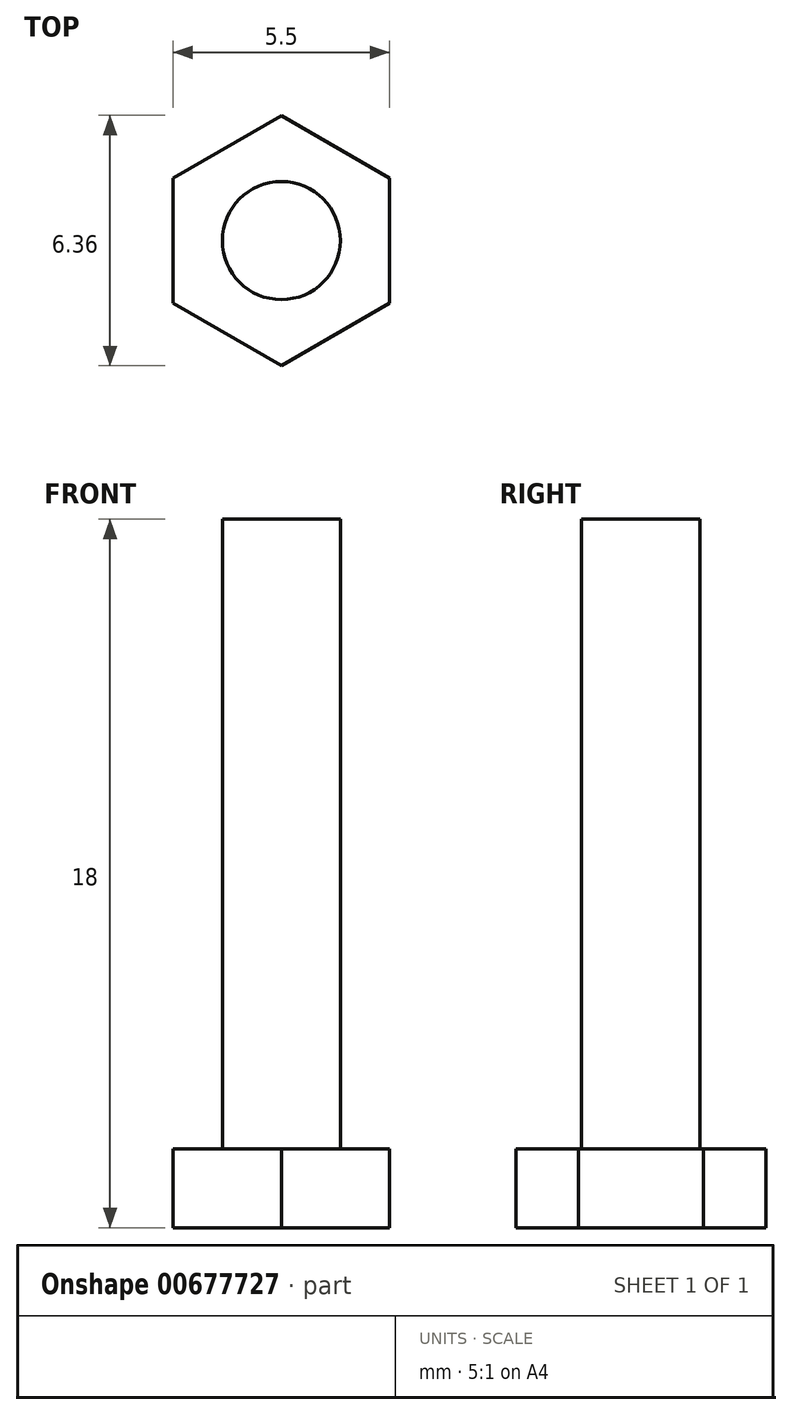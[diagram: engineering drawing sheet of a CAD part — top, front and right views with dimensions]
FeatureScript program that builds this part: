
annotation { "Feature Type Name" : "Feature", "Feature Type Description" : "" }
export const myFeature = defineFeature(function(context is Context, id is Id, definition is map)
    precondition{}
    {
        {
            var Q0;
            Q0=qCreatedBy(makeId("Top.planeOp"),FACE);
            var sketch = newSketch(context, id + "F0", { "sketchPlane" : qUnion([Q0])});
            skCircle(sketch, "E0.cCircle", {"center": v(0, 0) * mm, "radius": 2.75 * mm, "construction": true});
            skLineSegment(sketch, "E0.0", {"start": v(2.75, 1.59) * mm, "end": v(2.75, -1.59) * mm});
            skLineSegment(sketch, "E0.1", {"start": v(2.75, -1.59) * mm, "end": v(0, -3.18) * mm});
            skLineSegment(sketch, "E0.2", {"start": v(0, -3.18) * mm, "end": v(-2.75, -1.59) * mm});
            skLineSegment(sketch, "E0.3", {"start": v(-2.75, -1.59) * mm, "end": v(-2.75, 1.59) * mm});
            skLineSegment(sketch, "E0.4", {"start": v(-2.75, 1.59) * mm, "end": v(0, 3.18) * mm});
            skLineSegment(sketch, "E0.5", {"start": v(0, 3.18) * mm, "end": v(2.75, 1.59) * mm});
            skPoint(sketch, "E0.0.midPoint", {"position": v(2.75, 0) * mm});
            skSolve(sketch);
        }
        {
            var Q0;
            Q0=makeQuery(id+"F0.imprint","IMPRINT",FACE,{"disambiguationData":[TD([[makeQuery(id+"F0.imprint","IMPRINT",EDGE,{"derivedFrom":sQuery(id+"F0.wireOp",EDGE,"E0.0")}),-1.0]])]});
            extrude(context, id + "F1", {"entities" : qUnion([Q0]), "depth" : 2 * mm, "offsetDistance" : 25.4 * mm});
        }
        {
            var Q0;
            Q0=makeQuery(id+"F1.opExtrude","CAP_FACE",FACE,{"disambiguationData":[OSD([sQuery(id+"F0.wireOp",EDGE,"E0.0"),sQuery(id+"F0.wireOp",EDGE,"E0.1"),sQuery(id+"F0.wireOp",EDGE,"E0.2"),sQuery(id+"F0.wireOp",EDGE,"E0.3"),sQuery(id+"F0.wireOp",EDGE,"E0.4"),sQuery(id+"F0.wireOp",EDGE,"E0.5")])],"isStart":false});
            var sketch = newSketch(context, id + "F2", { "sketchPlane" : qUnion([Q0])});
            skLineSegment(sketch, "E1.0.0", {"start": v(2.75, 1.59) * mm, "end": v(0, 3.18) * mm});
            skLineSegment(sketch, "E1.0.1", {"start": v(0, 3.18) * mm, "end": v(-2.75, 1.59) * mm});
            skLineSegment(sketch, "E1.0.2", {"start": v(-2.75, 1.59) * mm, "end": v(-2.75, -1.59) * mm});
            skLineSegment(sketch, "E1.0.3", {"start": v(-2.75, -1.59) * mm, "end": v(0, -3.18) * mm});
            skLineSegment(sketch, "E1.0.4", {"start": v(0, -3.18) * mm, "end": v(2.75, -1.59) * mm});
            skLineSegment(sketch, "E1.0.5", {"start": v(2.75, -1.59) * mm, "end": v(2.75, 1.59) * mm});
            skLineSegment(sketch, "E2", {"start": v(-1.38, 2.38) * mm, "end": v(1.37, -2.38) * mm});
            skCircle(sketch, "E3", {"center": v(0, 0) * mm, "radius": 1.5 * mm});
            skSolve(sketch);
        }
        {
            var Q0;
            {var subQ0=sQuery(id+"F2.wireOp",EDGE,"E3");var subQ1=sQuery(id+"F2.wireOp",EDGE,"E2");var subQ2=makeQuery(id+"F2.imprint","INTERSECT",VERTEX,{"disambiguationData":[OD(0.0)],"derivedFrom":[subQ1,subQ0]});Q0=makeQuery(id+"F2.imprint","IMPRINT",FACE,{"disambiguationData":[TD([[makeQuery(id+"F2.imprint","IMPRINT",EDGE,{"disambiguationData":[TD([[subQ2,-1.0]])],"derivedFrom":subQ1}),1.0]])]});}
            var Q1;
            {var subQ0=sQuery(id+"F2.wireOp",EDGE,"E3");var subQ1=sQuery(id+"F2.wireOp",EDGE,"E2");var subQ2=makeQuery(id+"F2.imprint","INTERSECT",VERTEX,{"disambiguationData":[OD(0.0)],"derivedFrom":[subQ1,subQ0]});Q1=makeQuery(id+"F2.imprint","IMPRINT",FACE,{"disambiguationData":[TD([[makeQuery(id+"F2.imprint","IMPRINT",EDGE,{"disambiguationData":[TD([[subQ2,-1.0]])],"derivedFrom":subQ1}),-1.0]])]});}
            extrude(context, id + "F3", {"entities" : qUnion([Q0, Q1]), "operationType" : NewBodyOperationType.ADD, "depth" : 16 * mm, "offsetDistance" : 25.4 * mm});
        }
    });
